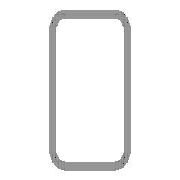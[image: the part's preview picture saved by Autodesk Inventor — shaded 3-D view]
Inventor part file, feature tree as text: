
AUTODESK INVENTOR PART (.ipt)
format: ipt  version: 2025 (Build 290162010, 162A)  size: 132,608 bytes
history: native  units: mm (DEFAULTED — no unit token found)
features: other x4, sketch x1, plane x1
ambient origin geometry x8: Origin, YZ Plane, XZ Plane, XY Plane, X Axis, Y Axis, Z Axis, Center Point
bodies: Solid1 (feature_tree), Body (feature_tree)
feature tree (6):
  parser-record x1  (decoder bookkeeping rows leaked as tree rows — omitted from the tree; the rows remain in map.json)
  other  "Driven Length"
  other  "Start Plane"
  other  "End Plane"
  sketch  "Sketch3"  dims[d3=2450.0mm d4=0.0mm d7=6.0mm d9=40.0mm d11=80.0mm d12=3.0mm d13=-0.0mm d14=2450.0mm d15=20.0mm d16=40.0mm d17=90.0deg d18=2450.0mm]
  plane  "Work Plane3"
